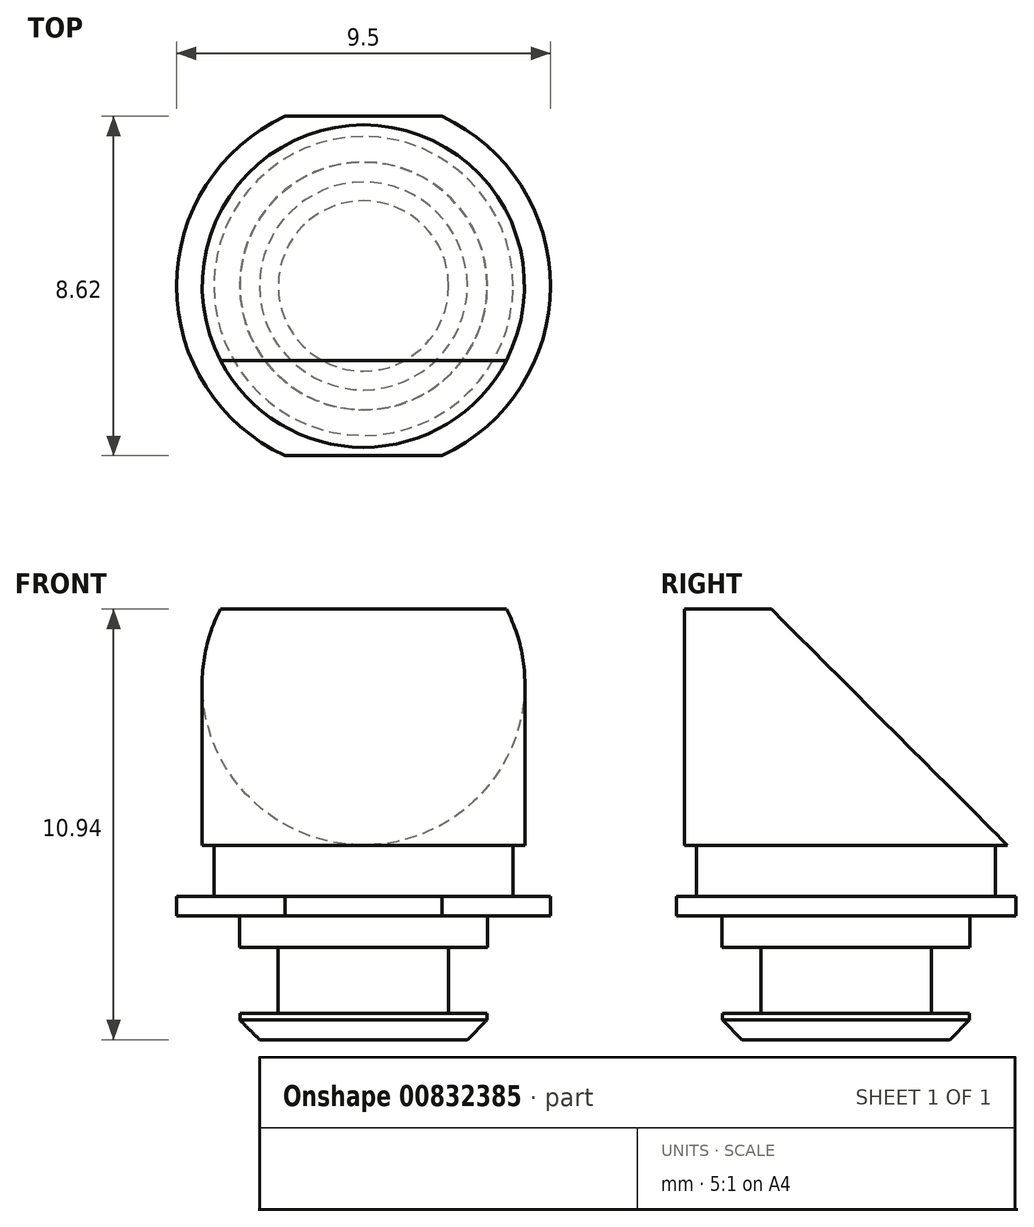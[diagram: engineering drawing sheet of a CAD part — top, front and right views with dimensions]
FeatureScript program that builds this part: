
annotation { "Feature Type Name" : "Feature", "Feature Type Description" : "" }
export const myFeature = defineFeature(function(context is Context, id is Id, definition is map)
    precondition{}
    {
        {
            var Q0;
            Q0=qCreatedBy(makeId("Top.planeOp"),FACE);
            var sketch = newSketch(context, id + "F0", { "sketchPlane" : qUnion([Q0])});
            skCircle(sketch, "E0", {"center": v(0, 0) * mm, "radius": 4.75 * mm});
            skSolve(sketch);
        }
        {
            var Q0;
            Q0=qSketchRegion(id+"F0",true);
            extrude(context, id + "F1", {"entities" : qUnion([Q0]), "depth" : 0.5 * mm});
        }
        {
            var Q0;
            Q0=makeQuery(id+"F1.opExtrude","CAP_FACE",FACE,{"disambiguationData":[OSD([sQuery(id+"F0.wireOp",EDGE,"E0")])],"isStart":false});
            var sketch = newSketch(context, id + "F2", { "sketchPlane" : qUnion([Q0])});
            skCircle(sketch, "E1", {"center": v(0, 0) * mm, "radius": 3.8 * mm});
            skSolve(sketch);
        }
        {
            var Q0;
            Q0=qSketchRegion(id+"F2",true);
            extrude(context, id + "F3", {"entities" : qUnion([Q0]), "operationType" : NewBodyOperationType.ADD, "depth" : 1.3 * mm});
        }
        {
            var Q0;
            Q0=makeQuery(id+"F1.opExtrude","CAP_FACE",FACE,{"disambiguationData":[OSD([sQuery(id+"F0.wireOp",EDGE,"E0")])],"isStart":true});
            var sketch = newSketch(context, id + "F4", { "sketchPlane" : qUnion([Q0])});
            skLineSegment(sketch, "E2", {"start": v(0, 4.3) * mm, "end": v(-2, 4.3) * mm});
            skLineSegment(sketch, "E3", {"start": v(-2, 4.3) * mm, "end": v(2, 4.3) * mm});
            skLineSegment(sketch, "E4", {"start": v(0, -4.3) * mm, "end": v(2, -4.3) * mm});
            skLineSegment(sketch, "E5", {"start": v(2, -4.3) * mm, "end": v(-2, -4.3) * mm});
            skSolve(sketch);
        }
        {
            var Q0;
            Q0=qSketchRegion(id+"F4",true);
            var Q1;
            {var subQ0=sQuery(id+"F4.wireOp",EDGE,"E3");var subQ3=makeQuery(id+"F4.imprint","IMPRINT",VERTEX,{"derivedFrom":subQ0});Q1=makeQuery(id+"F4.imprint","IMPRINT",FACE,{"disambiguationData":[TD([[makeQuery(id+"F4.imprint","IMPRINT",EDGE,{"disambiguationData":[TD([[subQ3,1.0]])],"derivedFrom":subQ0}),1.0]])]});}
            var Q2;
            {var subQ0=sQuery(id+"F4.wireOp",EDGE,"E5");var subQ3=makeQuery(id+"F4.imprint","IMPRINT",VERTEX,{"derivedFrom":subQ0});Q2=makeQuery(id+"F4.imprint","IMPRINT",FACE,{"disambiguationData":[TD([[makeQuery(id+"F4.imprint","IMPRINT",EDGE,{"disambiguationData":[TD([[subQ3,1.0]])],"derivedFrom":subQ0}),1.0]])]});}
            extrude(context, id + "F5", {"entities" : qUnion([Q0, Q1, Q2]), "operationType" : NewBodyOperationType.REMOVE, "endBound" : BoundingType.THROUGH_ALL, "oppositeDirection" : true, "offsetDistance" : 25 * mm, "depth" : 25 * mm});
        }
        {
            var Q0;
            Q0=makeQuery(id+"F1.opExtrude","CAP_FACE",FACE,{"disambiguationData":[OSD([sQuery(id+"F0.wireOp",EDGE,"E0")])],"isStart":true});
            var sketch = newSketch(context, id + "F6", { "sketchPlane" : qUnion([Q0])});
            skCircle(sketch, "E6", {"center": v(0, 0) * mm, "radius": 3.15 * mm});
            skSolve(sketch);
        }
        {
            var Q0;
            Q0=qSketchRegion(id+"F6",true);
            extrude(context, id + "F7", {"entities" : qUnion([Q0]), "operationType" : NewBodyOperationType.ADD, "depth" : 0.8 * mm});
        }
        {
            var Q0;
            Q0=makeQuery(id+"F7.opExtrude","CAP_FACE",FACE,{"disambiguationData":[OSD([sQuery(id+"F6.wireOp",EDGE,"E6")])],"isStart":false});
            var sketch = newSketch(context, id + "F8", { "sketchPlane" : qUnion([Q0])});
            skCircle(sketch, "E7", {"center": v(0, 0) * mm, "radius": 2.17 * mm});
            skSolve(sketch);
        }
        {
            var Q0;
            Q0=qSketchRegion(id+"F8",true);
            extrude(context, id + "F9", {"entities" : qUnion([Q0]), "operationType" : NewBodyOperationType.ADD, "depth" : 1.67 * mm});
        }
        {
            var Q0;
            Q0=makeQuery(id+"F9.opExtrude","CAP_FACE",FACE,{"disambiguationData":[OSD([sQuery(id+"F8.wireOp",EDGE,"E7")])],"isStart":false});
            var sketch = newSketch(context, id + "F10", { "sketchPlane" : qUnion([Q0])});
            skCircle(sketch, "E8.0", {"center": v(0, 0) * mm, "radius": 3.14 * mm});
            skSolve(sketch);
        }
        {
            var Q0;
            Q0=qSketchRegion(id+"F10",true);
            extrude(context, id + "F11", {"entities" : qUnion([Q0]), "operationType" : NewBodyOperationType.ADD, "depth" : 0.67 * mm});
        }
        {
            var Q0;
            Q0=makeQuery(id+"F11.opExtrude","CAP_EDGE",EDGE,{"disambiguationData":[OSD([sQuery(id+"F10.wireOp",EDGE,"E8.0")])],"isStart":false});
            chamfer(context, id + "F12", {"entities" : qUnion([Q0]), "width" : 0.5 * mm, "tangentPropagation" : true});
        }
        {
            var Q0;
            Q0=makeQuery(id+"F3.opExtrude","CAP_FACE",FACE,{"disambiguationData":[OSD([sQuery(id+"F2.wireOp",EDGE,"E1")])],"isStart":false});
            var sketch = newSketch(context, id + "F13", { "sketchPlane" : qUnion([Q0])});
            skLineSegment(sketch, "E9.bottom", {"start": v(4.1, 4.1) * mm, "end": v(-4.1, 4.1) * mm});
            skLineSegment(sketch, "E9.top", {"start": v(4.1, -4.1) * mm, "end": v(-4.1, -4.1) * mm});
            skLineSegment(sketch, "E9.left", {"start": v(4.1, 4.1) * mm, "end": v(4.1, -4.1) * mm});
            skLineSegment(sketch, "E9.right", {"start": v(-4.1, 4.1) * mm, "end": v(-4.1, -4.1) * mm});
            skPoint(sketch, "E9.middle", {"position": v(0, 0) * mm});
            skSolve(sketch);
        }
        {
            var Q0;
            Q0=makeQuery(id+"F13.imprint","IMPRINT",FACE,{"disambiguationData":[TD([[makeQuery(id+"F13.imprint","IMPRINT",EDGE,{"derivedFrom":sQuery(id+"F13.wireOp",EDGE,"E9.bottom")}),1.0]])]});
            var Q1;
            Q1=makeQuery(id+"F13.imprint","IMPRINT",FACE,{"disambiguationData":[TD([[makeQuery(id+"F13.imprint","IMPRINT",EDGE,{"derivedFrom":makeQuery(id+"F3.opExtrude","CAP_EDGE",EDGE,{"disambiguationData":[OSD([sQuery(id+"F2.wireOp",EDGE,"E1")])],"isStart":false})}),1.0]])]});
            extrude(context, id + "F14", {"entities" : qUnion([Q0, Q1]), "operationType" : NewBodyOperationType.ADD, "depth" : 6 * mm, "offsetDistance" : 25 * mm});
        }
        {
            var Q0;
            Q0=makeQuery(id+"F14.opExtrude","CAP_EDGE",EDGE,{"disambiguationData":[OSD([sQuery(id+"F13.wireOp",EDGE,"E9.bottom")])],"isStart":false});
            chamfer(context, id + "F15", {"entities" : qUnion([Q0]), "width" : 6 * mm, "tangentPropagation" : true});
        }
        {
            var Q0;
            Q0=makeQuery(id+"F14.opExtrude","CAP_FACE",FACE,{"disambiguationData":[OSD([sQuery(id+"F13.wireOp",EDGE,"E9.bottom"),sQuery(id+"F13.wireOp",EDGE,"E9.top"),sQuery(id+"F13.wireOp",EDGE,"E9.left"),sQuery(id+"F13.wireOp",EDGE,"E9.right")])],"isStart":true});
            var sketch = newSketch(context, id + "F16", { "sketchPlane" : qUnion([Q0])});
            skCircle(sketch, "E10", {"center": v(0, 0) * mm, "radius": 4.1 * mm});
            skSolve(sketch);
        }
        {
            var Q0;
            {var subQ0=sQuery(id+"F16.wireOp",EDGE,"E10");var subQ1=makeQuery(id+"F14.opExtrude","CAP_EDGE",EDGE,{"disambiguationData":[OSD([sQuery(id+"F13.wireOp",EDGE,"E9.top")])],"isStart":true});var subQ2=makeQuery(id+"F16.imprint","INTERSECT",VERTEX,{"derivedFrom":[subQ1,subQ0]});Q0=makeQuery(id+"F16.imprint","IMPRINT",FACE,{"disambiguationData":[TD([[makeQuery(id+"F16.imprint","IMPRINT",EDGE,{"disambiguationData":[TD([[subQ2,1.0]])],"derivedFrom":subQ0}),-1.0]])]});}
            var Q1;
            {var subQ0=sQuery(id+"F16.wireOp",EDGE,"E10");var subQ1=sQuery(id+"F13.wireOp",EDGE,"E9.left");var subQ2=makeQuery(id+"F14.opExtrude","CAP_EDGE",EDGE,{"disambiguationData":[OSD([subQ1])],"isStart":true});var subQ3=makeQuery(id+"F16.imprint","INTERSECT",VERTEX,{"derivedFrom":[subQ2,subQ0]});Q1=makeQuery(id+"F16.imprint","IMPRINT",FACE,{"disambiguationData":[TD([[makeQuery(id+"F16.imprint","IMPRINT",EDGE,{"disambiguationData":[TD([[subQ3,1.0]])],"derivedFrom":subQ0}),-1.0]])]});}
            var Q2;
            {var subQ0=sQuery(id+"F16.wireOp",EDGE,"E10");var subQ1=makeQuery(id+"F14.opExtrude","CAP_EDGE",EDGE,{"disambiguationData":[OSD([sQuery(id+"F13.wireOp",EDGE,"E9.top")])],"isStart":true});var subQ2=makeQuery(id+"F16.imprint","INTERSECT",VERTEX,{"derivedFrom":[subQ1,subQ0]});Q2=makeQuery(id+"F16.imprint","IMPRINT",FACE,{"disambiguationData":[TD([[makeQuery(id+"F16.imprint","IMPRINT",EDGE,{"disambiguationData":[TD([[subQ2,-1.0]])],"derivedFrom":subQ0}),-1.0]])]});}
            var Q3;
            {var subQ0=sQuery(id+"F16.wireOp",EDGE,"E10");var subQ1=sQuery(id+"F13.wireOp",EDGE,"E9.right");var subQ2=makeQuery(id+"F14.opExtrude","CAP_EDGE",EDGE,{"disambiguationData":[OSD([subQ1])],"isStart":true});var subQ3=makeQuery(id+"F16.imprint","INTERSECT",VERTEX,{"derivedFrom":[subQ2,subQ0]});Q3=makeQuery(id+"F16.imprint","IMPRINT",FACE,{"disambiguationData":[TD([[makeQuery(id+"F16.imprint","IMPRINT",EDGE,{"disambiguationData":[TD([[subQ3,-1.0]])],"derivedFrom":subQ0}),-1.0]])]});}
            extrude(context, id + "F17", {"entities" : qUnion([Q0, Q1, Q2, Q3]), "operationType" : NewBodyOperationType.REMOVE, "endBound" : BoundingType.THROUGH_ALL, "oppositeDirection" : true, "depth" : 25 * mm, "offsetDistance" : 25 * mm});
        }
    });
